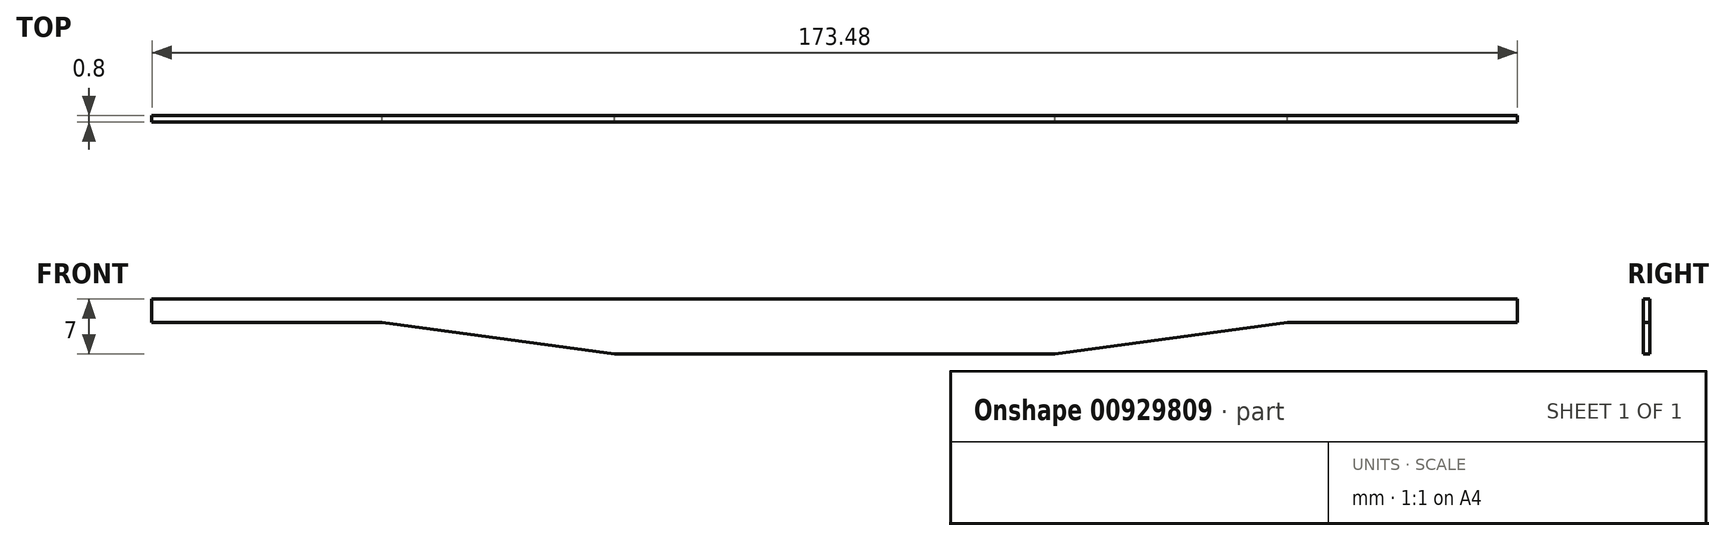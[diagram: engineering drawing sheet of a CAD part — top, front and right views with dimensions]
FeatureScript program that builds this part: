
annotation { "Feature Type Name" : "Feature", "Feature Type Description" : "" }
export const myFeature = defineFeature(function(context is Context, id is Id, definition is map)
    precondition{}
    {
        {
            var Q0;
            Q0=qCreatedBy(makeId("Front.planeOp"), FACE);
            var sketch = newSketch(context, id + "F0", { "sketchPlane" : qUnion([Q0])});
            skLineSegment(sketch, "E0", {"start": v(-59.34, 0) * mm, "end": v(114.14, 0) * mm});
            skLineSegment(sketch, "E1", {"start": v(114.14, 0) * mm, "end": v(114.14, -3) * mm});
            skLineSegment(sketch, "E2", {"start": v(114.14, -3) * mm, "end": v(84.9, -3) * mm});
            skLineSegment(sketch, "E3", {"start": v(84.9, -3) * mm, "end": v(55.4, -7) * mm});
            skLineSegment(sketch, "E4", {"start": v(55.4, -7) * mm, "end": v(-0.6, -7) * mm});
            skLineSegment(sketch, "E5", {"start": v(-0.6, -7) * mm, "end": v(-30.1, -3) * mm});
            skLineSegment(sketch, "E6", {"start": v(-30.1, -3) * mm, "end": v(-59.34, -3) * mm});
            skLineSegment(sketch, "E7", {"start": v(-59.34, -3) * mm, "end": v(-59.34, 0) * mm});
            skSolve(sketch);
        }
        {
            var Q0;
            Q0 = qSketchRegion(id + "F0", true);
            extrude(context, id + "F1", {"entities" : qUnion([Q0]), "depth" : 0.8 * mm, "offsetDistance" : 25 * mm});
        }
    });
